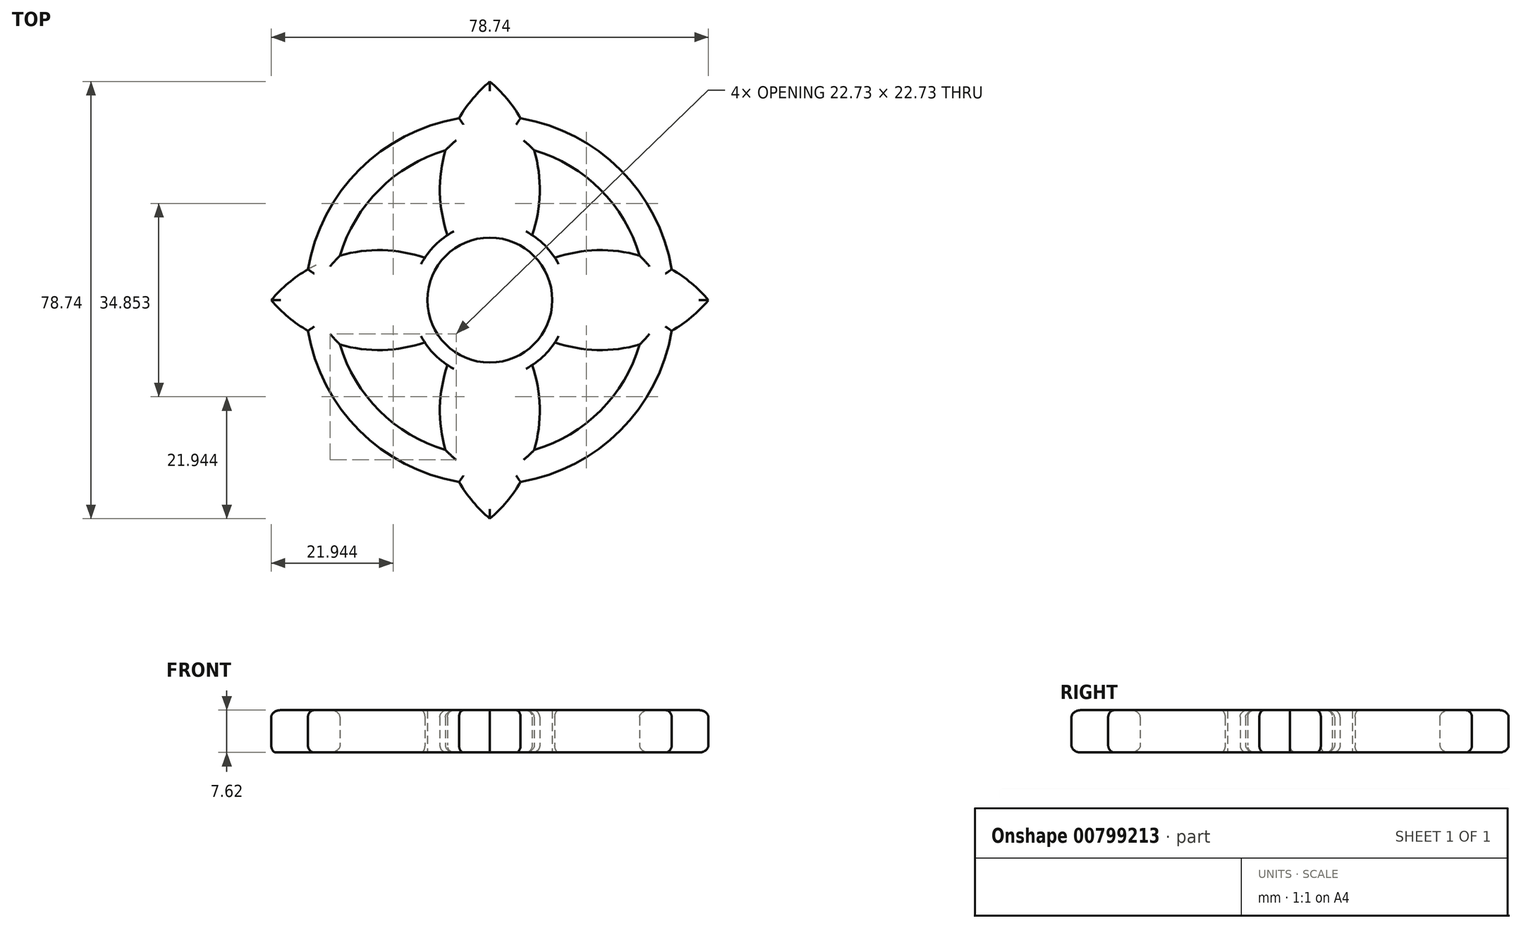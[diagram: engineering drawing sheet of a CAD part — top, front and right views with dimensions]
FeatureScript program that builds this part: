
annotation { "Feature Type Name" : "Feature", "Feature Type Description" : "" }
export const myFeature = defineFeature(function(context is Context, id is Id, definition is map)
    precondition{}
    {
        {
            var Q0;
            Q0=qCreatedBy(makeId("Top.planeOp"),FACE);
            var sketch = newSketch(context, id + "F0", { "sketchPlane" : qUnion([Q0])});
            skCircle(sketch, "E0", {"center": v(0, 0) * mm, "radius": 11.25 * mm});
            skCircle(sketch, "E1", {"center": v(0, 0) * mm, "radius": 13.97 * mm});
            skArc(sketch, "E2", {"start": v(0, 39.37) * mm, "mid": v(-8.09, 26.72) * mm, "end": v(-7.62, 11.7) * mm});
            skArc(sketch, "E3", {"start": v(7.62, 11.7) * mm, "mid": v(8.09, 26.72) * mm, "end": v(0, 39.37) * mm});
            skArc(sketch, "E4.1.0", {"start": v(-39.37, 0) * mm, "mid": v(-26.72, -8.09) * mm, "end": v(-11.7, -7.62) * mm});
            skArc(sketch, "E4.1.1", {"start": v(-11.7, 7.62) * mm, "mid": v(-26.72, 8.09) * mm, "end": v(-39.37, 0) * mm});
            skArc(sketch, "E4.2.0", {"start": v(0, -39.37) * mm, "mid": v(8.09, -26.72) * mm, "end": v(7.62, -11.7) * mm});
            skArc(sketch, "E4.2.1", {"start": v(-7.62, -11.7) * mm, "mid": v(-8.09, -26.72) * mm, "end": v(0, -39.37) * mm});
            skArc(sketch, "E5.3.3.0", {"start": v(39.37, 0) * mm, "mid": v(26.72, 8.09) * mm, "end": v(11.7, 7.62) * mm});
            skArc(sketch, "E5.4.3.0", {"start": v(11.7, -7.62) * mm, "mid": v(26.72, -8.09) * mm, "end": v(39.37, 0) * mm});
            skCircle(sketch, "E6", {"center": v(0, 0) * mm, "radius": 33.23 * mm});
            skCircle(sketch, "E7", {"center": v(0, 0) * mm, "radius": 28.15 * mm});
            skSolve(sketch);
        }
        {
            var Q0;
            {var subQ0=sQuery(id+"F0.wireOp",EDGE,"E6");var subQ1=sQuery(id+"F0.wireOp",EDGE,"E4.1.0");var subQ2=makeQuery(id+"F0.imprint","INTERSECT",VERTEX,{"derivedFrom":[subQ1,subQ0]});Q0=makeQuery(id+"F0.imprint","IMPRINT",FACE,{"disambiguationData":[TD([[makeQuery(id+"F0.imprint","IMPRINT",EDGE,{"disambiguationData":[TD([[subQ2,-1.0]])],"derivedFrom":subQ1}),-1.0]])]});}
            var Q1;
            {var subQ0=sQuery(id+"F0.wireOp",EDGE,"E4.1.1");var subQ1=sQuery(id+"F0.wireOp",EDGE,"E4.1.0");var subQ2=makeQuery(id+"F0.imprint","INTERSECT",VERTEX,{"derivedFrom":[subQ1,subQ0]});Q1=makeQuery(id+"F0.imprint","IMPRINT",FACE,{"disambiguationData":[TD([[makeQuery(id+"F0.imprint","IMPRINT",EDGE,{"disambiguationData":[TD([[subQ2,-1.0]])],"derivedFrom":subQ1}),1.0]])]});}
            var Q2;
            {var subQ0=sQuery(id+"F0.wireOp",EDGE,"E6");var subQ1=sQuery(id+"F0.wireOp",EDGE,"E4.1.0");var subQ2=makeQuery(id+"F0.imprint","INTERSECT",VERTEX,{"derivedFrom":[subQ1,subQ0]});Q2=makeQuery(id+"F0.imprint","IMPRINT",FACE,{"disambiguationData":[TD([[makeQuery(id+"F0.imprint","IMPRINT",EDGE,{"disambiguationData":[TD([[subQ2,-1.0]])],"derivedFrom":subQ1}),1.0]])]});}
            var Q3;
            {var subQ0=sQuery(id+"F0.wireOp",EDGE,"E4.1.0");var subQ1=sQuery(id+"F0.wireOp",EDGE,"E1");var subQ2=makeQuery(id+"F0.imprint","INTERSECT",VERTEX,{"derivedFrom":[subQ1,subQ0]});Q3=makeQuery(id+"F0.imprint","IMPRINT",FACE,{"disambiguationData":[TD([[makeQuery(id+"F0.imprint","IMPRINT",EDGE,{"disambiguationData":[TD([[subQ2,1.0]])],"derivedFrom":subQ1}),-1.0]])]});}
            var Q4;
            {var subQ0=sQuery(id+"F0.wireOp",EDGE,"E6");var subQ1=sQuery(id+"F0.wireOp",EDGE,"E2");var subQ2=makeQuery(id+"F0.imprint","INTERSECT",VERTEX,{"derivedFrom":[subQ1,subQ0]});Q4=makeQuery(id+"F0.imprint","IMPRINT",FACE,{"disambiguationData":[TD([[makeQuery(id+"F0.imprint","IMPRINT",EDGE,{"disambiguationData":[TD([[subQ2,-1.0]])],"derivedFrom":subQ1}),-1.0]])]});}
            var Q5;
            {var subQ0=sQuery(id+"F0.wireOp",EDGE,"E2");var subQ1=sQuery(id+"F0.wireOp",EDGE,"E1");var subQ2=makeQuery(id+"F0.imprint","INTERSECT",VERTEX,{"derivedFrom":[subQ1,subQ0]});Q5=makeQuery(id+"F0.imprint","IMPRINT",FACE,{"disambiguationData":[TD([[makeQuery(id+"F0.imprint","IMPRINT",EDGE,{"disambiguationData":[TD([[subQ2,1.0]])],"derivedFrom":subQ1}),-1.0]])]});}
            var Q6;
            Q6=makeQuery(id+"F0.imprint","IMPRINT",FACE,{"disambiguationData":[TD([[makeQuery(id+"F0.imprint","IMPRINT",EDGE,{"derivedFrom":sQuery(id+"F0.wireOp",EDGE,"E0")}),-1.0]])]});
            var Q7;
            {var subQ0=sQuery(id+"F0.wireOp",EDGE,"E4.2.0");var subQ1=sQuery(id+"F0.wireOp",EDGE,"E1");var subQ2=makeQuery(id+"F0.imprint","INTERSECT",VERTEX,{"derivedFrom":[subQ1,subQ0]});Q7=makeQuery(id+"F0.imprint","IMPRINT",FACE,{"disambiguationData":[TD([[makeQuery(id+"F0.imprint","IMPRINT",EDGE,{"disambiguationData":[TD([[subQ2,1.0]])],"derivedFrom":subQ1}),-1.0]])]});}
            var Q8;
            {var subQ0=sQuery(id+"F0.wireOp",EDGE,"E4.2.1");var subQ1=sQuery(id+"F0.wireOp",EDGE,"E4.2.0");var subQ2=makeQuery(id+"F0.imprint","INTERSECT",VERTEX,{"derivedFrom":[subQ1,subQ0]});Q8=makeQuery(id+"F0.imprint","IMPRINT",FACE,{"disambiguationData":[TD([[makeQuery(id+"F0.imprint","IMPRINT",EDGE,{"disambiguationData":[TD([[subQ2,-1.0]])],"derivedFrom":subQ1}),1.0]])]});}
            var Q9;
            {var subQ0=sQuery(id+"F0.wireOp",EDGE,"E6");var subQ1=sQuery(id+"F0.wireOp",EDGE,"E4.2.0");var subQ2=makeQuery(id+"F0.imprint","INTERSECT",VERTEX,{"derivedFrom":[subQ1,subQ0]});Q9=makeQuery(id+"F0.imprint","IMPRINT",FACE,{"disambiguationData":[TD([[makeQuery(id+"F0.imprint","IMPRINT",EDGE,{"disambiguationData":[TD([[subQ2,-1.0]])],"derivedFrom":subQ1}),1.0]])]});}
            var Q10;
            {var subQ0=sQuery(id+"F0.wireOp",EDGE,"E6");var subQ1=sQuery(id+"F0.wireOp",EDGE,"E4.2.0");var subQ2=makeQuery(id+"F0.imprint","INTERSECT",VERTEX,{"derivedFrom":[subQ1,subQ0]});Q10=makeQuery(id+"F0.imprint","IMPRINT",FACE,{"disambiguationData":[TD([[makeQuery(id+"F0.imprint","IMPRINT",EDGE,{"disambiguationData":[TD([[subQ2,-1.0]])],"derivedFrom":subQ1}),-1.0]])]});}
            var Q11;
            {var subQ0=sQuery(id+"F0.wireOp",EDGE,"E5.3.3.0");var subQ1=sQuery(id+"F0.wireOp",EDGE,"E1");var subQ2=makeQuery(id+"F0.imprint","INTERSECT",VERTEX,{"derivedFrom":[subQ1,subQ0]});Q11=makeQuery(id+"F0.imprint","IMPRINT",FACE,{"disambiguationData":[TD([[makeQuery(id+"F0.imprint","IMPRINT",EDGE,{"disambiguationData":[TD([[subQ2,1.0]])],"derivedFrom":subQ1}),-1.0]])]});}
            var Q12;
            {var subQ0=sQuery(id+"F0.wireOp",EDGE,"E6");var subQ1=sQuery(id+"F0.wireOp",EDGE,"E5.3.3.0");var subQ2=makeQuery(id+"F0.imprint","INTERSECT",VERTEX,{"derivedFrom":[subQ1,subQ0]});Q12=makeQuery(id+"F0.imprint","IMPRINT",FACE,{"disambiguationData":[TD([[makeQuery(id+"F0.imprint","IMPRINT",EDGE,{"disambiguationData":[TD([[subQ2,-1.0]])],"derivedFrom":subQ1}),1.0]])]});}
            var Q13;
            {var subQ0=sQuery(id+"F0.wireOp",EDGE,"E5.4.3.0");var subQ1=sQuery(id+"F0.wireOp",EDGE,"E5.3.3.0");var subQ2=makeQuery(id+"F0.imprint","INTERSECT",VERTEX,{"derivedFrom":[subQ1,subQ0]});Q13=makeQuery(id+"F0.imprint","IMPRINT",FACE,{"disambiguationData":[TD([[makeQuery(id+"F0.imprint","IMPRINT",EDGE,{"disambiguationData":[TD([[subQ2,-1.0]])],"derivedFrom":subQ1}),1.0]])]});}
            var Q14;
            {var subQ0=sQuery(id+"F0.wireOp",EDGE,"E6");var subQ1=sQuery(id+"F0.wireOp",EDGE,"E3");var subQ2=makeQuery(id+"F0.imprint","INTERSECT",VERTEX,{"derivedFrom":[subQ1,subQ0]});Q14=makeQuery(id+"F0.imprint","IMPRINT",FACE,{"disambiguationData":[TD([[makeQuery(id+"F0.imprint","IMPRINT",EDGE,{"disambiguationData":[TD([[subQ2,1.0]])],"derivedFrom":subQ1}),-1.0]])]});}
            var Q15;
            {var subQ0=sQuery(id+"F0.wireOp",EDGE,"E6");var subQ1=sQuery(id+"F0.wireOp",EDGE,"E2");var subQ2=makeQuery(id+"F0.imprint","INTERSECT",VERTEX,{"derivedFrom":[subQ1,subQ0]});Q15=makeQuery(id+"F0.imprint","IMPRINT",FACE,{"disambiguationData":[TD([[makeQuery(id+"F0.imprint","IMPRINT",EDGE,{"disambiguationData":[TD([[subQ2,-1.0]])],"derivedFrom":subQ1}),1.0]])]});}
            var Q16;
            {var subQ0=sQuery(id+"F0.wireOp",EDGE,"E3");var subQ1=sQuery(id+"F0.wireOp",EDGE,"E2");var subQ2=makeQuery(id+"F0.imprint","INTERSECT",VERTEX,{"derivedFrom":[subQ1,subQ0]});Q16=makeQuery(id+"F0.imprint","IMPRINT",FACE,{"disambiguationData":[TD([[makeQuery(id+"F0.imprint","IMPRINT",EDGE,{"disambiguationData":[TD([[subQ2,-1.0]])],"derivedFrom":subQ1}),1.0]])]});}
            extrude(context, id + "F1", {"entities" : qUnion([Q0, Q1, Q2, Q3, Q4, Q5, Q6, Q7, Q8, Q9, Q10, Q11, Q12, Q13, Q14, Q15, Q16]), "depth" : 7.62 * mm, "offsetDistance" : 25.4 * mm});
        }
        {
            var Q0;
            {var subQ0=sQuery(id+"F0.wireOp",EDGE,"E7");Q0=makeQuery(id+"F1.opExtrude","CAP_EDGE",EDGE,{"disambiguationData":[OSD([subQ0]),TDD([makeQuery(id+"F0.imprint","IMPRINT",EDGE,{"disambiguationData":[TD([[makeQuery(id+"F0.imprint","INTERSECT",VERTEX,{"derivedFrom":[sQuery(id+"F0.wireOp",EDGE,"E4.1.0"),subQ0]}),-1.0]])],"derivedFrom":subQ0})])],"isStart":false});}
            var Q1;
            {var subQ0=sQuery(id+"F0.wireOp",EDGE,"E7");Q1=makeQuery(id+"F1.opExtrude","CAP_EDGE",EDGE,{"disambiguationData":[OSD([subQ0]),TDD([makeQuery(id+"F0.imprint","IMPRINT",EDGE,{"disambiguationData":[TD([[makeQuery(id+"F0.imprint","INTERSECT",VERTEX,{"derivedFrom":[sQuery(id+"F0.wireOp",EDGE,"E2"),subQ0]}),-1.0]])],"derivedFrom":subQ0})])],"isStart":false});}
            var Q2;
            {var subQ0=sQuery(id+"F0.wireOp",EDGE,"E7");Q2=makeQuery(id+"F1.opExtrude","CAP_EDGE",EDGE,{"disambiguationData":[OSD([subQ0]),TDD([makeQuery(id+"F0.imprint","IMPRINT",EDGE,{"disambiguationData":[TD([[makeQuery(id+"F0.imprint","INTERSECT",VERTEX,{"derivedFrom":[sQuery(id+"F0.wireOp",EDGE,"E3"),subQ0]}),1.0]])],"derivedFrom":subQ0})])],"isStart":false});}
            var Q3;
            {var subQ0=sQuery(id+"F0.wireOp",EDGE,"E7");Q3=makeQuery(id+"F1.opExtrude","CAP_EDGE",EDGE,{"disambiguationData":[OSD([subQ0]),TDD([makeQuery(id+"F0.imprint","IMPRINT",EDGE,{"disambiguationData":[TD([[makeQuery(id+"F0.imprint","INTERSECT",VERTEX,{"derivedFrom":[sQuery(id+"F0.wireOp",EDGE,"E4.2.0"),subQ0]}),-1.0]])],"derivedFrom":subQ0})])],"isStart":false});}
            var Q4;
            {var subQ0=sQuery(id+"F0.wireOp",EDGE,"E4.2.0");Q4=makeQuery(id+"F1.opExtrude","CAP_EDGE",EDGE,{"disambiguationData":[OSD([subQ0]),TDD([makeQuery(id+"F0.imprint","IMPRINT",EDGE,{"disambiguationData":[TD([[makeQuery(id+"F0.imprint","INTERSECT",VERTEX,{"derivedFrom":[sQuery(id+"F0.wireOp",EDGE,"E1"),subQ0]}),1.0]])],"derivedFrom":subQ0})])],"isStart":false});}
            var Q5;
            {var subQ0=sQuery(id+"F0.wireOp",EDGE,"E4.2.1");Q5=makeQuery(id+"F1.opExtrude","CAP_EDGE",EDGE,{"disambiguationData":[OSD([subQ0]),TDD([makeQuery(id+"F0.imprint","IMPRINT",EDGE,{"disambiguationData":[TD([[makeQuery(id+"F0.imprint","INTERSECT",VERTEX,{"derivedFrom":[sQuery(id+"F0.wireOp",EDGE,"E1"),subQ0]}),-1.0]])],"derivedFrom":subQ0})])],"isStart":false});}
            var Q6;
            {var subQ0=sQuery(id+"F0.wireOp",EDGE,"E4.1.0");Q6=makeQuery(id+"F1.opExtrude","CAP_EDGE",EDGE,{"disambiguationData":[OSD([subQ0]),TDD([makeQuery(id+"F0.imprint","IMPRINT",EDGE,{"disambiguationData":[TD([[makeQuery(id+"F0.imprint","INTERSECT",VERTEX,{"derivedFrom":[sQuery(id+"F0.wireOp",EDGE,"E1"),subQ0]}),1.0]])],"derivedFrom":subQ0})])],"isStart":false});}
            var Q7;
            {var subQ0=sQuery(id+"F0.wireOp",EDGE,"E4.1.1");Q7=makeQuery(id+"F1.opExtrude","CAP_EDGE",EDGE,{"disambiguationData":[OSD([subQ0]),TDD([makeQuery(id+"F0.imprint","IMPRINT",EDGE,{"disambiguationData":[TD([[makeQuery(id+"F0.imprint","INTERSECT",VERTEX,{"derivedFrom":[sQuery(id+"F0.wireOp",EDGE,"E1"),subQ0]}),-1.0]])],"derivedFrom":subQ0})])],"isStart":false});}
            var Q8;
            {var subQ0=sQuery(id+"F0.wireOp",EDGE,"E2");Q8=makeQuery(id+"F1.opExtrude","CAP_EDGE",EDGE,{"disambiguationData":[OSD([subQ0]),TDD([makeQuery(id+"F0.imprint","IMPRINT",EDGE,{"disambiguationData":[TD([[makeQuery(id+"F0.imprint","INTERSECT",VERTEX,{"derivedFrom":[sQuery(id+"F0.wireOp",EDGE,"E1"),subQ0]}),1.0]])],"derivedFrom":subQ0})])],"isStart":false});}
            var Q9;
            {var subQ0=sQuery(id+"F0.wireOp",EDGE,"E3");Q9=makeQuery(id+"F1.opExtrude","CAP_EDGE",EDGE,{"disambiguationData":[OSD([subQ0]),TDD([makeQuery(id+"F0.imprint","IMPRINT",EDGE,{"disambiguationData":[TD([[makeQuery(id+"F0.imprint","INTERSECT",VERTEX,{"derivedFrom":[sQuery(id+"F0.wireOp",EDGE,"E1"),subQ0]}),-1.0]])],"derivedFrom":subQ0})])],"isStart":false});}
            var Q10;
            {var subQ0=sQuery(id+"F0.wireOp",EDGE,"E5.3.3.0");Q10=makeQuery(id+"F1.opExtrude","CAP_EDGE",EDGE,{"disambiguationData":[OSD([subQ0]),TDD([makeQuery(id+"F0.imprint","IMPRINT",EDGE,{"disambiguationData":[TD([[makeQuery(id+"F0.imprint","INTERSECT",VERTEX,{"derivedFrom":[sQuery(id+"F0.wireOp",EDGE,"E1"),subQ0]}),1.0]])],"derivedFrom":subQ0})])],"isStart":false});}
            var Q11;
            {var subQ0=sQuery(id+"F0.wireOp",EDGE,"E5.4.3.0");Q11=makeQuery(id+"F1.opExtrude","CAP_EDGE",EDGE,{"disambiguationData":[OSD([subQ0]),TDD([makeQuery(id+"F0.imprint","IMPRINT",EDGE,{"disambiguationData":[TD([[makeQuery(id+"F0.imprint","INTERSECT",VERTEX,{"derivedFrom":[sQuery(id+"F0.wireOp",EDGE,"E1"),subQ0]}),-1.0]])],"derivedFrom":subQ0})])],"isStart":false});}
            var Q12;
            {var subQ0=sQuery(id+"F0.wireOp",EDGE,"E6");Q12=makeQuery(id+"F1.opExtrude","CAP_EDGE",EDGE,{"disambiguationData":[OSD([subQ0]),TDD([makeQuery(id+"F0.imprint","IMPRINT",EDGE,{"disambiguationData":[TD([[makeQuery(id+"F0.imprint","INTERSECT",VERTEX,{"derivedFrom":[sQuery(id+"F0.wireOp",EDGE,"E4.1.0"),subQ0]}),-1.0]])],"derivedFrom":subQ0})])],"isStart":false});}
            var Q13;
            {var subQ0=sQuery(id+"F0.wireOp",EDGE,"E6");Q13=makeQuery(id+"F1.opExtrude","CAP_EDGE",EDGE,{"disambiguationData":[OSD([subQ0]),TDD([makeQuery(id+"F0.imprint","IMPRINT",EDGE,{"disambiguationData":[TD([[makeQuery(id+"F0.imprint","INTERSECT",VERTEX,{"derivedFrom":[sQuery(id+"F0.wireOp",EDGE,"E4.2.0"),subQ0]}),-1.0]])],"derivedFrom":subQ0})])],"isStart":false});}
            var Q14;
            {var subQ0=sQuery(id+"F0.wireOp",EDGE,"E6");Q14=makeQuery(id+"F1.opExtrude","CAP_EDGE",EDGE,{"disambiguationData":[OSD([subQ0]),TDD([makeQuery(id+"F0.imprint","IMPRINT",EDGE,{"disambiguationData":[TD([[makeQuery(id+"F0.imprint","INTERSECT",VERTEX,{"derivedFrom":[sQuery(id+"F0.wireOp",EDGE,"E2"),subQ0]}),-1.0]])],"derivedFrom":subQ0})])],"isStart":false});}
            var Q15;
            {var subQ0=sQuery(id+"F0.wireOp",EDGE,"E6");Q15=makeQuery(id+"F1.opExtrude","CAP_EDGE",EDGE,{"disambiguationData":[OSD([subQ0]),TDD([makeQuery(id+"F0.imprint","IMPRINT",EDGE,{"disambiguationData":[TD([[makeQuery(id+"F0.imprint","INTERSECT",VERTEX,{"derivedFrom":[sQuery(id+"F0.wireOp",EDGE,"E3"),subQ0]}),1.0]])],"derivedFrom":subQ0})])],"isStart":false});}
            var Q16;
            {var subQ0=sQuery(id+"F0.wireOp",EDGE,"E5.4.3.0");Q16=makeQuery(id+"F1.opExtrude","CAP_EDGE",EDGE,{"disambiguationData":[OSD([subQ0]),TDD([makeQuery(id+"F0.imprint","IMPRINT",EDGE,{"disambiguationData":[TD([[makeQuery(id+"F0.imprint","INTERSECT",VERTEX,{"derivedFrom":[sQuery(id+"F0.wireOp",EDGE,"E5.3.3.0"),subQ0]}),1.0]])],"derivedFrom":subQ0})])],"isStart":false});}
            var Q17;
            {var subQ0=sQuery(id+"F0.wireOp",EDGE,"E4.1.0");Q17=makeQuery(id+"F1.opExtrude","CAP_EDGE",EDGE,{"disambiguationData":[OSD([subQ0]),TDD([makeQuery(id+"F0.imprint","IMPRINT",EDGE,{"disambiguationData":[TD([[makeQuery(id+"F0.imprint","INTERSECT",VERTEX,{"derivedFrom":[subQ0,sQuery(id+"F0.wireOp",EDGE,"E4.1.1")]}),-1.0]])],"derivedFrom":subQ0})])],"isStart":false});}
            var Q18;
            {var subQ0=sQuery(id+"F0.wireOp",EDGE,"E4.1.1");Q18=makeQuery(id+"F1.opExtrude","CAP_EDGE",EDGE,{"disambiguationData":[OSD([subQ0]),TDD([makeQuery(id+"F0.imprint","IMPRINT",EDGE,{"disambiguationData":[TD([[makeQuery(id+"F0.imprint","INTERSECT",VERTEX,{"derivedFrom":[sQuery(id+"F0.wireOp",EDGE,"E4.1.0"),subQ0]}),1.0]])],"derivedFrom":subQ0})])],"isStart":false});}
            var Q19;
            {var subQ0=sQuery(id+"F0.wireOp",EDGE,"E5.3.3.0");Q19=makeQuery(id+"F1.opExtrude","CAP_EDGE",EDGE,{"disambiguationData":[OSD([subQ0]),TDD([makeQuery(id+"F0.imprint","IMPRINT",EDGE,{"disambiguationData":[TD([[makeQuery(id+"F0.imprint","INTERSECT",VERTEX,{"derivedFrom":[subQ0,sQuery(id+"F0.wireOp",EDGE,"E5.4.3.0")]}),-1.0]])],"derivedFrom":subQ0})])],"isStart":false});}
            var Q20;
            {var subQ0=sQuery(id+"F0.wireOp",EDGE,"E2");Q20=makeQuery(id+"F1.opExtrude","CAP_EDGE",EDGE,{"disambiguationData":[OSD([subQ0]),TDD([makeQuery(id+"F0.imprint","IMPRINT",EDGE,{"disambiguationData":[TD([[makeQuery(id+"F0.imprint","INTERSECT",VERTEX,{"derivedFrom":[subQ0,sQuery(id+"F0.wireOp",EDGE,"E3")]}),-1.0]])],"derivedFrom":subQ0})])],"isStart":false});}
            var Q21;
            {var subQ0=sQuery(id+"F0.wireOp",EDGE,"E3");Q21=makeQuery(id+"F1.opExtrude","CAP_EDGE",EDGE,{"disambiguationData":[OSD([subQ0]),TDD([makeQuery(id+"F0.imprint","IMPRINT",EDGE,{"disambiguationData":[TD([[makeQuery(id+"F0.imprint","INTERSECT",VERTEX,{"derivedFrom":[sQuery(id+"F0.wireOp",EDGE,"E2"),subQ0]}),1.0]])],"derivedFrom":subQ0})])],"isStart":false});}
            var Q22;
            {var subQ0=sQuery(id+"F0.wireOp",EDGE,"E4.2.1");Q22=makeQuery(id+"F1.opExtrude","CAP_EDGE",EDGE,{"disambiguationData":[OSD([subQ0]),TDD([makeQuery(id+"F0.imprint","IMPRINT",EDGE,{"disambiguationData":[TD([[makeQuery(id+"F0.imprint","INTERSECT",VERTEX,{"derivedFrom":[sQuery(id+"F0.wireOp",EDGE,"E4.2.0"),subQ0]}),1.0]])],"derivedFrom":subQ0})])],"isStart":false});}
            var Q23;
            {var subQ0=sQuery(id+"F0.wireOp",EDGE,"E4.2.0");Q23=makeQuery(id+"F1.opExtrude","CAP_EDGE",EDGE,{"disambiguationData":[OSD([subQ0]),TDD([makeQuery(id+"F0.imprint","IMPRINT",EDGE,{"disambiguationData":[TD([[makeQuery(id+"F0.imprint","INTERSECT",VERTEX,{"derivedFrom":[subQ0,sQuery(id+"F0.wireOp",EDGE,"E4.2.1")]}),-1.0]])],"derivedFrom":subQ0})])],"isStart":false});}
            var Q24;
            {var subQ0=sQuery(id+"F0.wireOp",EDGE,"E4.1.0");Q24=makeQuery(id+"F1.opExtrude","CAP_EDGE",EDGE,{"disambiguationData":[OSD([subQ0]),TDD([makeQuery(id+"F0.imprint","IMPRINT",EDGE,{"disambiguationData":[TD([[makeQuery(id+"F0.imprint","INTERSECT",VERTEX,{"derivedFrom":[subQ0,sQuery(id+"F0.wireOp",EDGE,"E4.1.1")]}),-1.0]])],"derivedFrom":subQ0})])],"isStart":true});}
            var Q25;
            {var subQ0=sQuery(id+"F0.wireOp",EDGE,"E6");Q25=makeQuery(id+"F1.opExtrude","CAP_EDGE",EDGE,{"disambiguationData":[OSD([subQ0]),TDD([makeQuery(id+"F0.imprint","IMPRINT",EDGE,{"disambiguationData":[TD([[makeQuery(id+"F0.imprint","INTERSECT",VERTEX,{"derivedFrom":[sQuery(id+"F0.wireOp",EDGE,"E4.1.0"),subQ0]}),-1.0]])],"derivedFrom":subQ0})])],"isStart":true});}
            var Q26;
            {var subQ0=sQuery(id+"F0.wireOp",EDGE,"E4.2.1");Q26=makeQuery(id+"F1.opExtrude","CAP_EDGE",EDGE,{"disambiguationData":[OSD([subQ0]),TDD([makeQuery(id+"F0.imprint","IMPRINT",EDGE,{"disambiguationData":[TD([[makeQuery(id+"F0.imprint","INTERSECT",VERTEX,{"derivedFrom":[sQuery(id+"F0.wireOp",EDGE,"E4.2.0"),subQ0]}),1.0]])],"derivedFrom":subQ0})])],"isStart":true});}
            var Q27;
            {var subQ0=sQuery(id+"F0.wireOp",EDGE,"E4.2.0");Q27=makeQuery(id+"F1.opExtrude","CAP_EDGE",EDGE,{"disambiguationData":[OSD([subQ0]),TDD([makeQuery(id+"F0.imprint","IMPRINT",EDGE,{"disambiguationData":[TD([[makeQuery(id+"F0.imprint","INTERSECT",VERTEX,{"derivedFrom":[subQ0,sQuery(id+"F0.wireOp",EDGE,"E4.2.1")]}),-1.0]])],"derivedFrom":subQ0})])],"isStart":true});}
            var Q28;
            {var subQ0=sQuery(id+"F0.wireOp",EDGE,"E6");Q28=makeQuery(id+"F1.opExtrude","CAP_EDGE",EDGE,{"disambiguationData":[OSD([subQ0]),TDD([makeQuery(id+"F0.imprint","IMPRINT",EDGE,{"disambiguationData":[TD([[makeQuery(id+"F0.imprint","INTERSECT",VERTEX,{"derivedFrom":[sQuery(id+"F0.wireOp",EDGE,"E4.2.0"),subQ0]}),-1.0]])],"derivedFrom":subQ0})])],"isStart":true});}
            var Q29;
            {var subQ0=sQuery(id+"F0.wireOp",EDGE,"E5.4.3.0");Q29=makeQuery(id+"F1.opExtrude","CAP_EDGE",EDGE,{"disambiguationData":[OSD([subQ0]),TDD([makeQuery(id+"F0.imprint","IMPRINT",EDGE,{"disambiguationData":[TD([[makeQuery(id+"F0.imprint","INTERSECT",VERTEX,{"derivedFrom":[sQuery(id+"F0.wireOp",EDGE,"E5.3.3.0"),subQ0]}),1.0]])],"derivedFrom":subQ0})])],"isStart":true});}
            var Q30;
            {var subQ0=sQuery(id+"F0.wireOp",EDGE,"E5.3.3.0");Q30=makeQuery(id+"F1.opExtrude","CAP_EDGE",EDGE,{"disambiguationData":[OSD([subQ0]),TDD([makeQuery(id+"F0.imprint","IMPRINT",EDGE,{"disambiguationData":[TD([[makeQuery(id+"F0.imprint","INTERSECT",VERTEX,{"derivedFrom":[subQ0,sQuery(id+"F0.wireOp",EDGE,"E5.4.3.0")]}),-1.0]])],"derivedFrom":subQ0})])],"isStart":true});}
            var Q31;
            {var subQ0=sQuery(id+"F0.wireOp",EDGE,"E6");Q31=makeQuery(id+"F1.opExtrude","CAP_EDGE",EDGE,{"disambiguationData":[OSD([subQ0]),TDD([makeQuery(id+"F0.imprint","IMPRINT",EDGE,{"disambiguationData":[TD([[makeQuery(id+"F0.imprint","INTERSECT",VERTEX,{"derivedFrom":[sQuery(id+"F0.wireOp",EDGE,"E3"),subQ0]}),1.0]])],"derivedFrom":subQ0})])],"isStart":true});}
            var Q32;
            {var subQ0=sQuery(id+"F0.wireOp",EDGE,"E3");Q32=makeQuery(id+"F1.opExtrude","CAP_EDGE",EDGE,{"disambiguationData":[OSD([subQ0]),TDD([makeQuery(id+"F0.imprint","IMPRINT",EDGE,{"disambiguationData":[TD([[makeQuery(id+"F0.imprint","INTERSECT",VERTEX,{"derivedFrom":[sQuery(id+"F0.wireOp",EDGE,"E2"),subQ0]}),1.0]])],"derivedFrom":subQ0})])],"isStart":true});}
            var Q33;
            {var subQ0=sQuery(id+"F0.wireOp",EDGE,"E2");Q33=makeQuery(id+"F1.opExtrude","CAP_EDGE",EDGE,{"disambiguationData":[OSD([subQ0]),TDD([makeQuery(id+"F0.imprint","IMPRINT",EDGE,{"disambiguationData":[TD([[makeQuery(id+"F0.imprint","INTERSECT",VERTEX,{"derivedFrom":[subQ0,sQuery(id+"F0.wireOp",EDGE,"E3")]}),-1.0]])],"derivedFrom":subQ0})])],"isStart":true});}
            var Q34;
            {var subQ0=sQuery(id+"F0.wireOp",EDGE,"E6");Q34=makeQuery(id+"F1.opExtrude","CAP_EDGE",EDGE,{"disambiguationData":[OSD([subQ0]),TDD([makeQuery(id+"F0.imprint","IMPRINT",EDGE,{"disambiguationData":[TD([[makeQuery(id+"F0.imprint","INTERSECT",VERTEX,{"derivedFrom":[sQuery(id+"F0.wireOp",EDGE,"E2"),subQ0]}),-1.0]])],"derivedFrom":subQ0})])],"isStart":true});}
            var Q35;
            {var subQ0=sQuery(id+"F0.wireOp",EDGE,"E7");Q35=makeQuery(id+"F1.opExtrude","CAP_EDGE",EDGE,{"disambiguationData":[OSD([subQ0]),TDD([makeQuery(id+"F0.imprint","IMPRINT",EDGE,{"disambiguationData":[TD([[makeQuery(id+"F0.imprint","INTERSECT",VERTEX,{"derivedFrom":[sQuery(id+"F0.wireOp",EDGE,"E4.2.0"),subQ0]}),-1.0]])],"derivedFrom":subQ0})])],"isStart":true});}
            var Q36;
            {var subQ0=sQuery(id+"F0.wireOp",EDGE,"E7");Q36=makeQuery(id+"F1.opExtrude","CAP_EDGE",EDGE,{"disambiguationData":[OSD([subQ0]),TDD([makeQuery(id+"F0.imprint","IMPRINT",EDGE,{"disambiguationData":[TD([[makeQuery(id+"F0.imprint","INTERSECT",VERTEX,{"derivedFrom":[sQuery(id+"F0.wireOp",EDGE,"E4.1.0"),subQ0]}),-1.0]])],"derivedFrom":subQ0})])],"isStart":true});}
            var Q37;
            {var subQ0=sQuery(id+"F0.wireOp",EDGE,"E3");Q37=makeQuery(id+"F1.opExtrude","CAP_EDGE",EDGE,{"disambiguationData":[OSD([subQ0]),TDD([makeQuery(id+"F0.imprint","IMPRINT",EDGE,{"disambiguationData":[TD([[makeQuery(id+"F0.imprint","INTERSECT",VERTEX,{"derivedFrom":[sQuery(id+"F0.wireOp",EDGE,"E1"),subQ0]}),-1.0]])],"derivedFrom":subQ0})])],"isStart":true});}
            var Q38;
            {var subQ0=sQuery(id+"F0.wireOp",EDGE,"E7");Q38=makeQuery(id+"F1.opExtrude","CAP_EDGE",EDGE,{"disambiguationData":[OSD([subQ0]),TDD([makeQuery(id+"F0.imprint","IMPRINT",EDGE,{"disambiguationData":[TD([[makeQuery(id+"F0.imprint","INTERSECT",VERTEX,{"derivedFrom":[sQuery(id+"F0.wireOp",EDGE,"E3"),subQ0]}),1.0]])],"derivedFrom":subQ0})])],"isStart":true});}
            var Q39;
            {var subQ0=sQuery(id+"F0.wireOp",EDGE,"E5.3.3.0");Q39=makeQuery(id+"F1.opExtrude","CAP_EDGE",EDGE,{"disambiguationData":[OSD([subQ0]),TDD([makeQuery(id+"F0.imprint","IMPRINT",EDGE,{"disambiguationData":[TD([[makeQuery(id+"F0.imprint","INTERSECT",VERTEX,{"derivedFrom":[sQuery(id+"F0.wireOp",EDGE,"E1"),subQ0]}),1.0]])],"derivedFrom":subQ0})])],"isStart":true});}
            var Q40;
            {var subQ0=sQuery(id+"F0.wireOp",EDGE,"E7");Q40=makeQuery(id+"F1.opExtrude","CAP_EDGE",EDGE,{"disambiguationData":[OSD([subQ0]),TDD([makeQuery(id+"F0.imprint","IMPRINT",EDGE,{"disambiguationData":[TD([[makeQuery(id+"F0.imprint","INTERSECT",VERTEX,{"derivedFrom":[sQuery(id+"F0.wireOp",EDGE,"E2"),subQ0]}),-1.0]])],"derivedFrom":subQ0})])],"isStart":true});}
            var Q41;
            {var subQ0=sQuery(id+"F0.wireOp",EDGE,"E2");Q41=makeQuery(id+"F1.opExtrude","CAP_EDGE",EDGE,{"disambiguationData":[OSD([subQ0]),TDD([makeQuery(id+"F0.imprint","IMPRINT",EDGE,{"disambiguationData":[TD([[makeQuery(id+"F0.imprint","INTERSECT",VERTEX,{"derivedFrom":[sQuery(id+"F0.wireOp",EDGE,"E1"),subQ0]}),1.0]])],"derivedFrom":subQ0})])],"isStart":true});}
            var Q42;
            {var subQ0=sQuery(id+"F0.wireOp",EDGE,"E4.1.1");Q42=makeQuery(id+"F1.opExtrude","CAP_EDGE",EDGE,{"disambiguationData":[OSD([subQ0]),TDD([makeQuery(id+"F0.imprint","IMPRINT",EDGE,{"disambiguationData":[TD([[makeQuery(id+"F0.imprint","INTERSECT",VERTEX,{"derivedFrom":[sQuery(id+"F0.wireOp",EDGE,"E1"),subQ0]}),-1.0]])],"derivedFrom":subQ0})])],"isStart":true});}
            var Q43;
            {var subQ0=sQuery(id+"F0.wireOp",EDGE,"E4.1.0");Q43=makeQuery(id+"F1.opExtrude","CAP_EDGE",EDGE,{"disambiguationData":[OSD([subQ0]),TDD([makeQuery(id+"F0.imprint","IMPRINT",EDGE,{"disambiguationData":[TD([[makeQuery(id+"F0.imprint","INTERSECT",VERTEX,{"derivedFrom":[sQuery(id+"F0.wireOp",EDGE,"E1"),subQ0]}),1.0]])],"derivedFrom":subQ0})])],"isStart":true});}
            var Q44;
            {var subQ0=sQuery(id+"F0.wireOp",EDGE,"E4.2.1");Q44=makeQuery(id+"F1.opExtrude","CAP_EDGE",EDGE,{"disambiguationData":[OSD([subQ0]),TDD([makeQuery(id+"F0.imprint","IMPRINT",EDGE,{"disambiguationData":[TD([[makeQuery(id+"F0.imprint","INTERSECT",VERTEX,{"derivedFrom":[sQuery(id+"F0.wireOp",EDGE,"E1"),subQ0]}),-1.0]])],"derivedFrom":subQ0})])],"isStart":true});}
            var Q45;
            {var subQ0=sQuery(id+"F0.wireOp",EDGE,"E5.4.3.0");Q45=makeQuery(id+"F1.opExtrude","CAP_EDGE",EDGE,{"disambiguationData":[OSD([subQ0]),TDD([makeQuery(id+"F0.imprint","IMPRINT",EDGE,{"disambiguationData":[TD([[makeQuery(id+"F0.imprint","INTERSECT",VERTEX,{"derivedFrom":[sQuery(id+"F0.wireOp",EDGE,"E1"),subQ0]}),-1.0]])],"derivedFrom":subQ0})])],"isStart":true});}
            var Q46;
            {var subQ0=sQuery(id+"F0.wireOp",EDGE,"E4.2.0");Q46=makeQuery(id+"F1.opExtrude","CAP_EDGE",EDGE,{"disambiguationData":[OSD([subQ0]),TDD([makeQuery(id+"F0.imprint","IMPRINT",EDGE,{"disambiguationData":[TD([[makeQuery(id+"F0.imprint","INTERSECT",VERTEX,{"derivedFrom":[sQuery(id+"F0.wireOp",EDGE,"E1"),subQ0]}),1.0]])],"derivedFrom":subQ0})])],"isStart":true});}
            fillet(context, id + "F2", {"entities" : qUnion([Q0, Q1, Q2, Q3, Q4, Q5, Q6, Q7, Q8, Q9, Q10, Q11, Q12, Q13, Q14, Q15, Q16, Q17, Q18, Q19, Q20, Q21, Q22, Q23, Q24, Q25, Q26, Q27, Q28, Q29, Q30, Q31, Q32, Q33, Q34, Q35, Q36, Q37, Q38, Q39, Q40, Q41, Q42, Q43, Q44, Q45, Q46]), "radius" : 1.27 * mm, "tangentPropagation" : true, "allowEdgeOverflow" : false});
        }
    });
